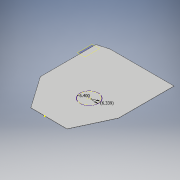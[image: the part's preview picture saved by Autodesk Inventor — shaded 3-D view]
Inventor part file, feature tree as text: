
AUTODESK INVENTOR PART (.ipt)
format: ipt  version: 2018 (Build 220112000, 112)  size: 130,560 bytes
history: native  units: in
note: dims shown in document units (in); Inventor stores cm internally (conversion verified against a paired STEP export)
features: other x9, reference x7, sketch x4, extrude x3, plane x1
ambient origin geometry x8: Origin, YZ Plane, XZ Plane, XY Plane, X Axis, Y Axis, Z Axis, Center Point
bodies: Solid1 (feature_tree)
feature tree (24):
  other  "Table"
  other  "side cover plate-01"
  other  "side cover plate-02"
  plane  "Work Plane1"
  extrude  "Plate extrude"  Depth=0.063in
  extrude  "Tailstock door"  Depth=0.063in TaperAngle=0.0deg
  extrude  "Headstock cut out"  Depth=6.3386in
  sketch  "Sketch5"  dims[d9=0.063in d10=0.0in]
  reference  "Reference2"
  reference  "Reference5"
  reference  "Reference6"
  sketch  "Sketch2"  dims[d0=0.063in d1=0.0in d3=11.811in]
  sketch  "Sketch3"  dims[d4=11.811in d5=0.063in d6=0.0in]
  reference  "Reference7"
  reference  "Reference8"
  sketch  "Sketch4"  dims[d7=6.4in d8=6.3386in]
  reference  "Reference9"
  reference  "Reference10"
  other  "Lathe Model 2018.iam"
  other  "front:1"
  other  "back plate:1"
  other  "Gearbox:1"
  other  "connecting wheel:1"
  other  "polycarbonate cover:1"
